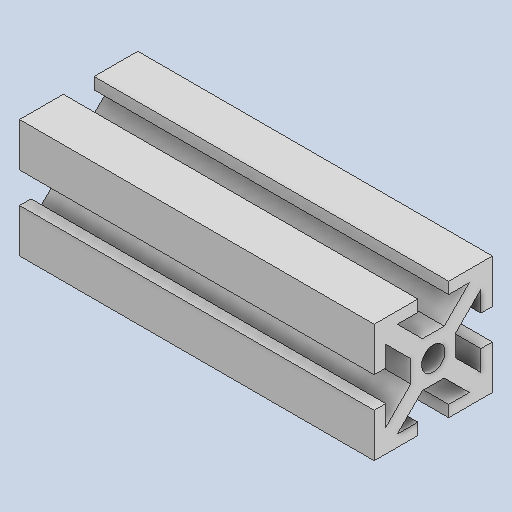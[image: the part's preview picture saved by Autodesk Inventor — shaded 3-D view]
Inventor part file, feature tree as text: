
AUTODESK INVENTOR PART (.ipt)
format: ipt  version: 2023 (Build 270158030, 158C)  size: 167,424 bytes
history: native  units: in
note: dims shown in document units (in); Inventor stores cm internally (conversion verified against a paired STEP export)
features: extrude x1, sketch x1
ambient origin geometry x8: Origin, YZ Plane, XZ Plane, XY Plane, X Axis, Y Axis, Z Axis, Center Point
bodies: Solid1 (feature_tree)
feature tree (2):
  extrude  "Extrusion1"  Depth=0.0975in
  sketch  "Sketch1"  dims[d2=0.37in d3=0.0975in d7=0.0975in d10=0.0975in d11=1.0in d13=0.0975in d16=0.0975in d17=0.37in d18=1.0in d23=0.0975in d24=1.0in d25=1.0in d32=0.175in d33=0.175in d35=135.0deg d36=0.175in d37=0.175in d38=0.0975in d40=0.175in d41=0.175in d42=0.175in d43=0.175in d44=0.2in d45=3.0in d46=0.0in]
